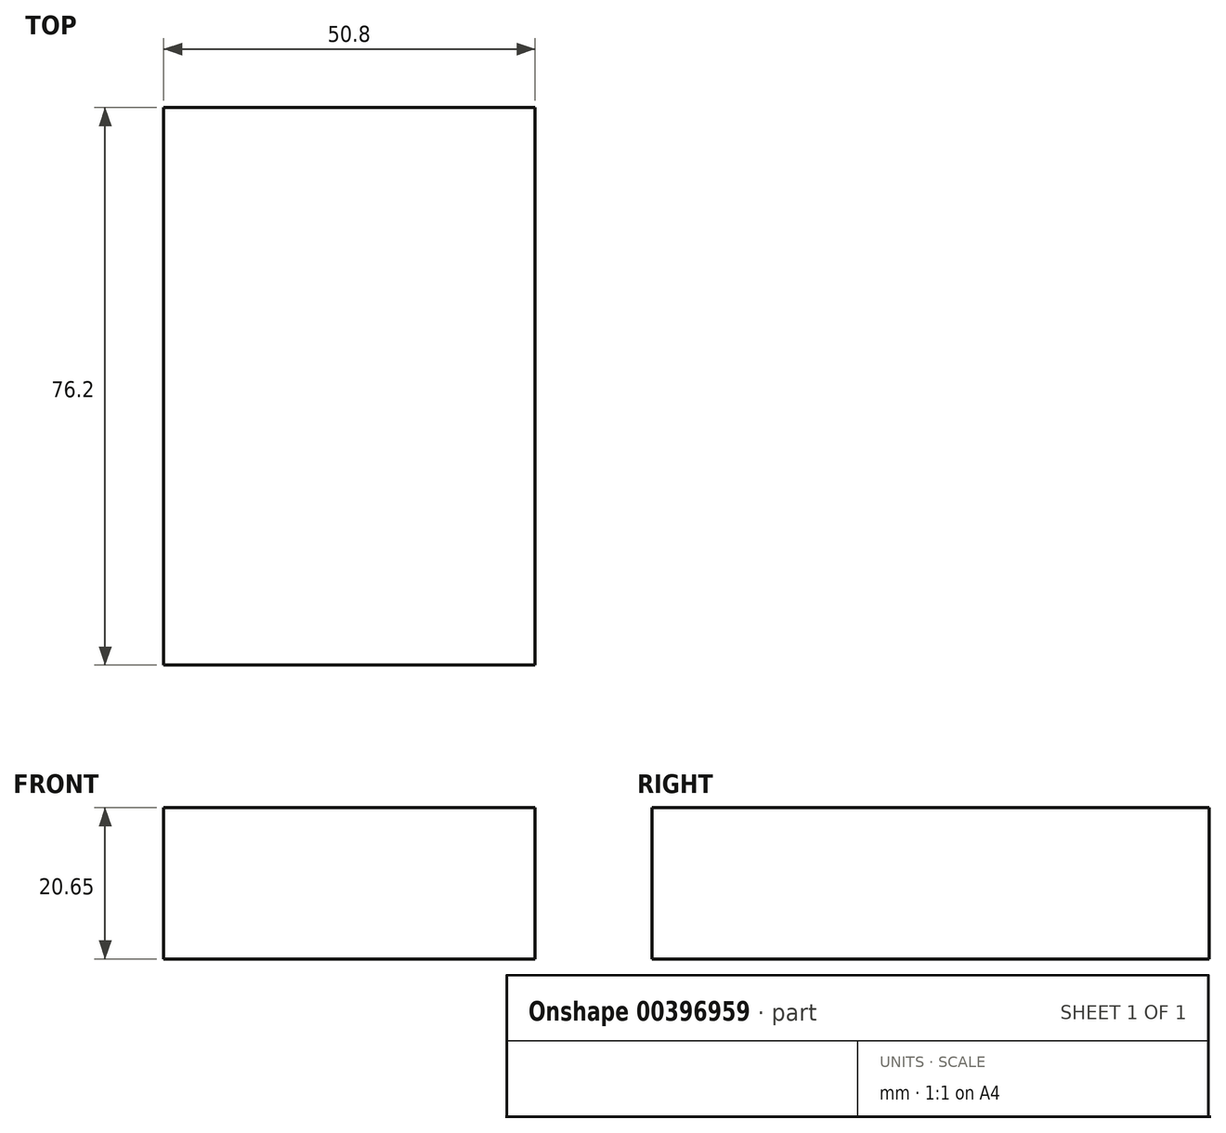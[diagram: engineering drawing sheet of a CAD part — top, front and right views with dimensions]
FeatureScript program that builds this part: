
annotation { "Feature Type Name" : "Feature", "Feature Type Description" : "" }
export const myFeature = defineFeature(function(context is Context, id is Id, definition is map)
    precondition{}
    {
        {
            var Q0;
            Q0=qCreatedBy(makeId("Top.planeOp"),FACE);
            var sketch = newSketch(context, id + "F0", { "sketchPlane" : qUnion([Q0])});
            skLineSegment(sketch, "E0.bottom", {"start": v(25.4, -38.1) * mm, "end": v(-25.4, -38.1) * mm});
            skLineSegment(sketch, "E0.top", {"start": v(25.4, 38.1) * mm, "end": v(-25.4, 38.1) * mm});
            skLineSegment(sketch, "E0.left", {"start": v(25.4, -38.1) * mm, "end": v(25.4, 38.1) * mm});
            skLineSegment(sketch, "E0.right", {"start": v(-25.4, -38.1) * mm, "end": v(-25.4, 38.1) * mm});
            skPoint(sketch, "E0.middle", {"position": v(0, 0) * mm});
            skSolve(sketch);
        }
        {
            var Q0;
            Q0 = qSketchRegion(id + "F0", true);
            extrude(context, id + "F1", {"entities" : qUnion([Q0]), "depth" : 20.65 * mm});
        }
    });
